# Revit family: VRUo
name_source: partatom
category: Lighting Fixtures
units: mm (PartAtom-declared; Revit-internal decimal feet)

## family parameters
Always vertical = Yes
Cut with Voids When Loaded = No
Host = Ceiling
Light Source = Yes
OmniClass Number = 23.80.70.11.14.17
OmniClass Title = Direct/Indirect
Part Type = Normal
Room Calculation Point = No
Round Connector Dimension = Use Diameter
Shared = No

## types (14) — shared parameters
Assembly Code = D5020200
Color Filter = 16777215
Description = LED Vandal Resistant Recessed Universal
Dimming Lamp Color Temperature Shift = <None>
Emit Shape Visible in Rendering = No
Housing Finish = Metal - Viscor - White
Lamp = LED
Lens1 Finish = Acrylic - Viscor - 0.040" White Frosted  with Polycarbonate Clear  0.125" Thick
Manufacturer = CERTOLUX by VISCOR
Model = VRU
Tilt Angle = 90.00°
URL = https://www.viscor.com
Voltage = 120 V

## per-type parameters (varying)
| type | Apparent Load | Emit from Rectangle Length | Emit from Rectangle Width | Lamp Wattage | Length | Lens2 Finish | Photometric Web File | Width |
| VRUo-1X4-LED840K035LUNV-P82P08 | 33 VA | 3' - 11 3/4" | 0' - 11 3/4" | 33 VA | 3' - 11 3/4" | Polycarbonate - Viscor - 0.156in Prismatic | VRUo-1X4-LED840K035LUNV-P82P08.ies | 0' - 11 3/4" |
| VRUo-2X2-LED840K035LUNV-P82P08 | 32 VA | 1' - 11 3/4" | 1' - 11 3/4" | 32 VA | 1' - 11 3/4" | <By Category> | VRUo-2X2-LED840K035LUNV-P82P08.ies | 1' - 11 3/4" |
| VRUo-2X4-LED840K055LUNV-P82P08 | 47 VA | 3' - 11 3/4" | 1' - 11 3/4" | 47 VA | 3' - 11 3/4" | <By Category> | VRUo-2X4-LED840K055LUNV-P82P08.ies | 1' - 11 3/4" |
| VRUo-1X4-LED840K055LUNV-P82P08 | 53 VA | 3' - 11 3/4" | 0' - 11 3/4" | 53 VA | 3' - 11 3/4" | <By Category> | VRUo-1X4-LED840K055LUNV-P82P08.ies | 0' - 11 3/4" |
| VRUo-1X4-LED840K070LUNV-P82P08 | 70 VA | 3' - 11 3/4" | 0' - 11 3/4" | 70 VA | 3' - 11 3/4" | <By Category> | VRUo-1X4-LED840K070LUNV-P82P08.ies | 0' - 11 3/4" |
| VRUo-1X4-LED840K100LUNV-P82P08 | 99 VA | 3' - 11 3/4" | 0' - 11 3/4" | 99 VA | 3' - 11 3/4" | <By Category> | VRUo-1X4-LED840K100LUNV-P82P08.ies | 0' - 11 3/4" |
| VRUo-2X2-LED840K055LUNV-P82P08 | 52 VA | 1' - 11 3/4" | 1' - 11 3/4" | 52 VA | 1' - 11 3/4" | <By Category> | VRUo-2X2-LED840K055LUNV-P82P08.ies | 1' - 11 3/4" |
| VRUo-2X2-LED840K070LUNV-P82P08 | 68 VA | 1' - 11 3/4" | 1' - 11 3/4" | 68 VA | 1' - 11 3/4" | <By Category> | VRUo-2X2-LED840K070LUNV-P82P08.ies | 1' - 11 3/4" |
| VRUo-2X2-LED840K100LUNV-P82P08 | 98 VA | 1' - 11 3/4" | 1' - 11 3/4" | 98 VA | 1' - 11 3/4" | <By Category> | VRUo-2X2-LED840K100LUNV-P82P08.ies | 1' - 11 3/4" |
| VRUo-2X4-LED840K070LUNV-P82P08 | 61 VA | 3' - 11 3/4" | 1' - 11 3/4" | 61 VA | 3' - 11 3/4" | <By Category> | VRUo-2X4-LED840K070LUNV-P82P08.ies | 1' - 11 3/4" |
| VRUo-2X4-LED840K100LUNV-P82P08 | 82 VA | 3' - 11 3/4" | 1' - 11 3/4" | 82 VA | 3' - 11 3/4" | <By Category> | VRUo-2X4-LED840K100LUNV-P82P08.ies | 1' - 11 3/4" |
| VRUo-2X4-LED840K120LUNV-P82P08 | 101 VA | 3' - 11 3/4" | 1' - 11 3/4" | 101 VA | 3' - 11 3/4" | <By Category> | VRUo-2X4-LED840K120LUNV-P82P08.ies | 1' - 11 3/4" |
| VRUo-2X4-LED840K180LUNV-P82P08 | 146 VA | 3' - 11 3/4" | 1' - 11 3/4" | 146 VA | 3' - 11 3/4" | <By Category> | VRUo-2X4-LED840K180LUNV-P82P08.ies | 1' - 11 3/4" |
| VRUo-2X4-LED840K240LUNV-P82P08 | 200 VA | 3' - 11 3/4" | 1' - 11 3/4" | 200 VA | 3' - 11 3/4" | <By Category> | VRUo-2X4 -LED840K240LUNV-P82P08.IES | 1' - 11 3/4" |

## geometry (parser evidence)
native form markers: Sweep x2
no freeform markers — native parametric forms only
